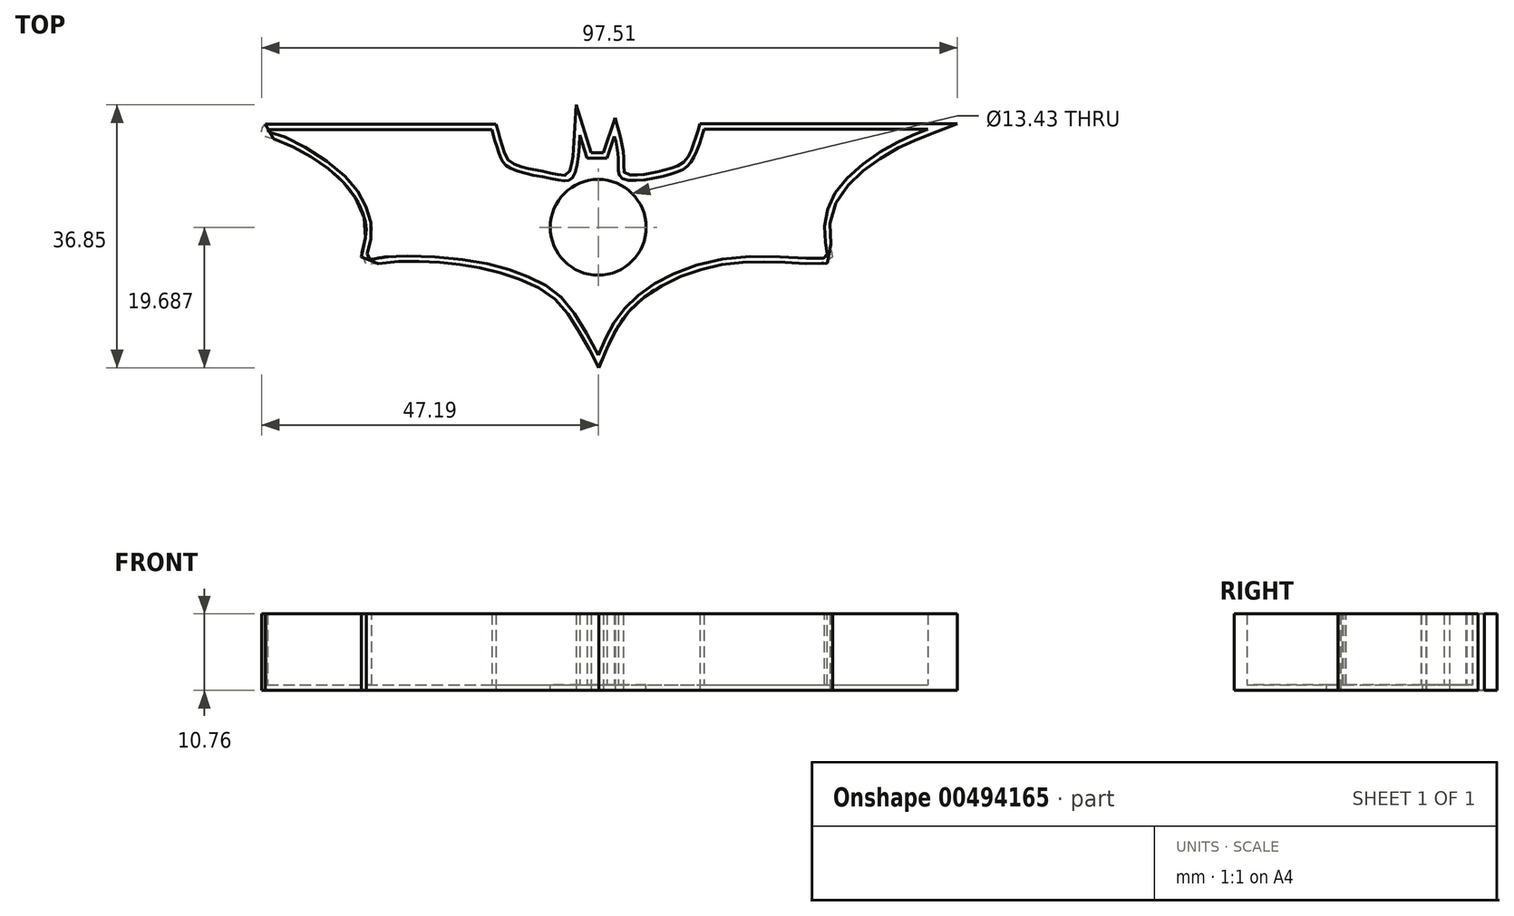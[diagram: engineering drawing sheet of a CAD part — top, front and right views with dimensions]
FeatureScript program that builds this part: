
annotation { "Feature Type Name" : "Feature", "Feature Type Description" : "" }
export const myFeature = defineFeature(function(context is Context, id is Id, definition is map)
    precondition{}
    {
        {
            var Q0;
            Q0=qCreatedBy(makeId("Top.planeOp"),FACE);
            var sketch = newSketch(context, id + "F0", { "sketchPlane" : qUnion([Q0])});
            skLineSegment(sketch, "E0", {"start": v(-46.32, 17.43) * mm, "end": v(-15.44, 17.43) * mm});
            skLineSegment(sketch, "E1", {"start": v(-2.57, 16.68) * mm, "end": v(-1.59, 13.49) * mm});
            skLineSegment(sketch, "E2", {"start": v(-1.59, 13.49) * mm, "end": v(-0.48, 13.49) * mm});
            skFitSpline(sketch, "E3", {"points": [v(-46.32, 17.43) * mm, v(-46.42, 17.24) * mm, v(-44.86, 16.77) * mm, v(-36.59, 11.96) * mm, v(-32.67, 6.96) * mm, v(-31.8, 2.5) * mm, v(-32.38, -0.57) * mm, v(-30.24, -0.46) * mm, v(-18.94, -0.75) * mm, v(-10.3, -2.95) * mm, v(-4.86, -6.43) * mm, v(0, -14.13) * mm], "startDerivative": vector(-9.3, -10.78) * mm, "endDerivative": vector(36.7, -70.39) * mm});
            skLineSegment(sketch, "E4", {"start": v(-0.48, 13.49) * mm, "end": v(0, 13.49) * mm});
            skLineSegment(sketch, "E5", {"start": v(-0.48, 13.49) * mm, "end": v(0.92, 13.49) * mm});
            skLineSegment(sketch, "E6", {"start": v(14.8, 17.5) * mm, "end": v(46.2, 17.5) * mm});
            skLineSegment(sketch, "E7", {"start": v(0.92, 13.49) * mm, "end": v(1.24, 13.49) * mm});
            skLineSegment(sketch, "E8", {"start": v(1.24, 13.49) * mm, "end": v(2.27, 16.52) * mm});
            skFitSpline(sketch, "E9", {"points": [v(2.27, 16.52) * mm, v(2.83, 13.28) * mm, v(3.28, 10.68) * mm, v(9.78, 11.13) * mm, v(12.96, 12.85) * mm, v(14.8, 17.5) * mm], "startDerivative": vector(4.75, -17.59) * mm, "endDerivative": vector(7.03, 24.32) * mm});
            skFitSpline(sketch, "E10", {"points": [v(0, -14.13) * mm, v(2.96, -8.49) * mm, v(8.81, -3.62) * mm, v(21.09, -0.33) * mm, v(31.9, -0.5) * mm, v(32.05, 0) * mm, v(31.7, 4.15) * mm, v(34.14, 9.82) * mm, v(40.92, 15.16) * mm, v(46.2, 17.5) * mm], "startDerivative": vector(22.61, 53.18) * mm, "endDerivative": vector(48.1, 18.4) * mm});
            skLineSegment(sketch, "E11", {"start": v(-15.44, 17.43) * mm, "end": v(-14.9, 17.43) * mm});
            skFitSpline(sketch, "E12", {"points": [v(-14.9, 17.43) * mm, v(-14.59, 16.28) * mm, v(-13.76, 13.72) * mm, v(-12.33, 12.05) * mm, v(-6.37, 10.55) * mm, v(-3.73, 10.58) * mm, v(-2.57, 16.68) * mm], "startDerivative": vector(2.64, -9.94) * mm, "endDerivative": vector(1.99, 34.36) * mm});
            skSolve(sketch);
        }
        {
            var Q0;
            Q0=makeQuery(id+"F0.imprint","IMPRINT",FACE,{"disambiguationData":[TD([[makeQuery(id+"F0.imprint","IMPRINT",EDGE,{"derivedFrom":sQuery(id+"F0.wireOp",EDGE,"E0")}),-1.0]])]});
            var sketch = newSketch(context, id + "F1", { "sketchPlane" : qUnion([Q0])});
            skCircle(sketch, "E13", {"center": v(0, 3.77) * mm, "radius": 6.71 * mm});
            skSolve(sketch);
        }
        {
            var Q0;
            Q0=makeQuery(id+"F0.imprint","IMPRINT",FACE,{"disambiguationData":[TD([[makeQuery(id+"F0.imprint","IMPRINT",EDGE,{"derivedFrom":sQuery(id+"F0.wireOp",EDGE,"E0")}),-1.0]])]});
            extrude(context, id + "F2", {"entities" : qUnion([Q0]), "depth" : 10 * mm});
        }
        {
            var Q0;
            Q0=makeQuery(id+"F2.opExtrude","CAP_FACE",FACE,{"disambiguationData":[OSD([sQuery(id+"F0.wireOp",EDGE,"E0"),sQuery(id+"F0.wireOp",EDGE,"E1"),sQuery(id+"F0.wireOp",EDGE,"E2"),sQuery(id+"F0.wireOp",EDGE,"E3"),sQuery(id+"F0.wireOp",EDGE,"E5"),sQuery(id+"F0.wireOp",EDGE,"E6"),sQuery(id+"F0.wireOp",EDGE,"E7"),sQuery(id+"F0.wireOp",EDGE,"E8"),sQuery(id+"F0.wireOp",EDGE,"E9"),sQuery(id+"F0.wireOp",EDGE,"E10"),sQuery(id+"F0.wireOp",EDGE,"E11"),sQuery(id+"F0.wireOp",EDGE,"E12")])],"isStart":false});
            shell(context, id + "F3", {"entities" : qUnion([Q0]), "thickness" : 0.76 * mm, "oppositeDirection" : true});
        }
        {
            var Q0;
            Q0=makeQuery(id+"F1.imprint","IMPRINT",FACE,{"disambiguationData":[TD([[makeQuery(id+"F1.imprint","IMPRINT",EDGE,{"derivedFrom":sQuery(id+"F1.wireOp",EDGE,"E13")}),1.0]])]});
            extrude(context, id + "F4", {"entities" : qUnion([Q0]), "operationType" : NewBodyOperationType.REMOVE, "oppositeDirection" : true, "depth" : 25.4 * mm});
        }
    });
